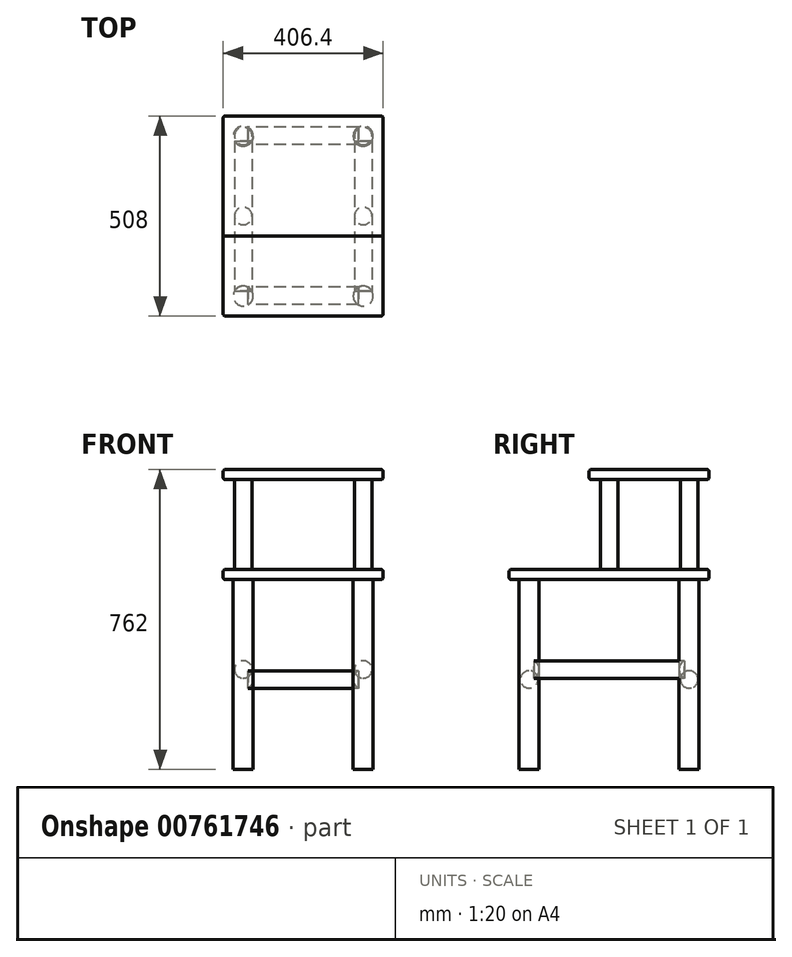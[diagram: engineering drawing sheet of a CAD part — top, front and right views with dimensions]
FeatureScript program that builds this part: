
annotation { "Feature Type Name" : "Feature", "Feature Type Description" : "" }
export const myFeature = defineFeature(function(context is Context, id is Id, definition is map)
    precondition{}
    {
        {
            var Q0;
            Q0=qCreatedBy(makeId("Top.planeOp"),FACE);
            var sketch = newSketch(context, id + "F0", { "sketchPlane" : qUnion([Q0])});
            skLineSegment(sketch, "E0.bottom", {"start": v(152.4, 203.2) * mm, "end": v(-152.4, 203.2) * mm});
            skLineSegment(sketch, "E0.top", {"start": v(152.4, -203.2) * mm, "end": v(-152.4, -203.2) * mm});
            skLineSegment(sketch, "E0.left", {"start": v(152.4, 203.2) * mm, "end": v(152.4, -203.2) * mm});
            skLineSegment(sketch, "E0.right", {"start": v(-152.4, 203.2) * mm, "end": v(-152.4, -203.2) * mm});
            skPoint(sketch, "E0.middle", {"position": v(0, 0) * mm});
            skCircle(sketch, "E1", {"center": v(-152.4, 203.2) * mm, "radius": 25.4 * mm});
            skCircle(sketch, "E2.MirrorC", {"center": v(152.4, 203.2) * mm, "radius": 25.4 * mm});
            skCircle(sketch, "E3.MirrorC", {"center": v(-152.4, -203.2) * mm, "radius": 25.4 * mm});
            skCircle(sketch, "E4.MirrorC", {"center": v(152.4, -203.2) * mm, "radius": 25.4 * mm});
            skSolve(sketch);
        }
        {
            var Q0;
            {var subQ0=sQuery(id+"F0.wireOp",EDGE,"E0.right");var subQ1=sQuery(id+"F0.wireOp",EDGE,"E0.bottom");var subQ2=makeQuery(id+"F0.imprint","INTERSECT",VERTEX,{"derivedFrom":[subQ1,subQ0]});Q0=makeQuery(id+"F0.imprint","IMPRINT",FACE,{"disambiguationData":[TD([[makeQuery(id+"F0.imprint","IMPRINT",EDGE,{"disambiguationData":[TD([[subQ2,1.0]])],"derivedFrom":subQ1}),1.0]])]});}
            var Q1;
            {var subQ0=sQuery(id+"F0.wireOp",EDGE,"E0.right");var subQ1=sQuery(id+"F0.wireOp",EDGE,"E0.bottom");var subQ2=makeQuery(id+"F0.imprint","INTERSECT",VERTEX,{"derivedFrom":[subQ1,subQ0]});Q1=makeQuery(id+"F0.imprint","IMPRINT",FACE,{"disambiguationData":[TD([[makeQuery(id+"F0.imprint","IMPRINT",EDGE,{"disambiguationData":[TD([[subQ2,1.0]])],"derivedFrom":subQ1}),-1.0]])]});}
            var Q2;
            {var subQ0=sQuery(id+"F0.wireOp",EDGE,"E0.left");var subQ1=sQuery(id+"F0.wireOp",EDGE,"E0.bottom");var subQ2=makeQuery(id+"F0.imprint","INTERSECT",VERTEX,{"derivedFrom":[subQ1,subQ0]});Q2=makeQuery(id+"F0.imprint","IMPRINT",FACE,{"disambiguationData":[TD([[makeQuery(id+"F0.imprint","IMPRINT",EDGE,{"disambiguationData":[TD([[subQ2,-1.0]])],"derivedFrom":subQ1}),-1.0]])]});}
            var Q3;
            {var subQ0=sQuery(id+"F0.wireOp",EDGE,"E0.left");var subQ1=sQuery(id+"F0.wireOp",EDGE,"E0.bottom");var subQ2=makeQuery(id+"F0.imprint","INTERSECT",VERTEX,{"derivedFrom":[subQ1,subQ0]});Q3=makeQuery(id+"F0.imprint","IMPRINT",FACE,{"disambiguationData":[TD([[makeQuery(id+"F0.imprint","IMPRINT",EDGE,{"disambiguationData":[TD([[subQ2,-1.0]])],"derivedFrom":subQ1}),1.0]])]});}
            var Q4;
            {var subQ0=sQuery(id+"F0.wireOp",EDGE,"E0.left");var subQ1=sQuery(id+"F0.wireOp",EDGE,"E0.top");var subQ2=makeQuery(id+"F0.imprint","INTERSECT",VERTEX,{"derivedFrom":[subQ1,subQ0]});Q4=makeQuery(id+"F0.imprint","IMPRINT",FACE,{"disambiguationData":[TD([[makeQuery(id+"F0.imprint","IMPRINT",EDGE,{"disambiguationData":[TD([[subQ2,-1.0]])],"derivedFrom":subQ1}),1.0]])]});}
            var Q5;
            {var subQ0=sQuery(id+"F0.wireOp",EDGE,"E0.left");var subQ1=sQuery(id+"F0.wireOp",EDGE,"E0.top");var subQ2=makeQuery(id+"F0.imprint","INTERSECT",VERTEX,{"derivedFrom":[subQ1,subQ0]});Q5=makeQuery(id+"F0.imprint","IMPRINT",FACE,{"disambiguationData":[TD([[makeQuery(id+"F0.imprint","IMPRINT",EDGE,{"disambiguationData":[TD([[subQ2,-1.0]])],"derivedFrom":subQ1}),-1.0]])]});}
            var Q6;
            {var subQ0=sQuery(id+"F0.wireOp",EDGE,"E0.right");var subQ1=sQuery(id+"F0.wireOp",EDGE,"E0.top");var subQ2=makeQuery(id+"F0.imprint","INTERSECT",VERTEX,{"derivedFrom":[subQ1,subQ0]});Q6=makeQuery(id+"F0.imprint","IMPRINT",FACE,{"disambiguationData":[TD([[makeQuery(id+"F0.imprint","IMPRINT",EDGE,{"disambiguationData":[TD([[subQ2,1.0]])],"derivedFrom":subQ1}),-1.0]])]});}
            var Q7;
            {var subQ0=sQuery(id+"F0.wireOp",EDGE,"E0.right");var subQ1=sQuery(id+"F0.wireOp",EDGE,"E0.top");var subQ2=makeQuery(id+"F0.imprint","INTERSECT",VERTEX,{"derivedFrom":[subQ1,subQ0]});Q7=makeQuery(id+"F0.imprint","IMPRINT",FACE,{"disambiguationData":[TD([[makeQuery(id+"F0.imprint","IMPRINT",EDGE,{"disambiguationData":[TD([[subQ2,1.0]])],"derivedFrom":subQ1}),1.0]])]});}
            extrude(context, id + "F1", {"entities" : qUnion([Q0, Q1, Q2, Q3, Q4, Q5, Q6, Q7]), "depth" : 482.6 * mm, "offsetDistance" : 25.4 * mm});
        }
        {
            var Q0;
            Q0=qCreatedBy(makeId("Top.planeOp"),FACE);
            cPlane(context, id + "F2", {"entities" : qUnion([Q0]), "cplaneType" : CPlaneType.OFFSET, "offset" : 482.6 * mm, "width" : 152.4 * mm, "height" : 152.4 * mm});
        }
        {
            var Q0;
            Q0=qCreatedBy(id+"F2.planeOp",FACE);
            var sketch = newSketch(context, id + "F3", { "sketchPlane" : qUnion([Q0])});
            skPoint(sketch, "E5.0", {"position": v(0, 0) * mm});
            skLineSegment(sketch, "E6.bottom", {"start": v(203.2, -254) * mm, "end": v(-203.2, -254) * mm});
            skLineSegment(sketch, "E6.top", {"start": v(203.2, 254) * mm, "end": v(-203.2, 254) * mm});
            skLineSegment(sketch, "E6.left", {"start": v(203.2, -254) * mm, "end": v(203.2, 254) * mm});
            skLineSegment(sketch, "E6.right", {"start": v(-203.2, -254) * mm, "end": v(-203.2, 254) * mm});
            skSolve(sketch);
        }
        {
            var Q0;
            Q0=makeQuery(id+"F3.imprint","IMPRINT",FACE,{"disambiguationData":[TD([[makeQuery(id+"F3.imprint","IMPRINT",EDGE,{"derivedFrom":sQuery(id+"F3.wireOp",EDGE,"E6.bottom")}),-1.0]])]});
            extrude(context, id + "F4", {"entities" : qUnion([Q0]), "depth" : 25.4 * mm, "offsetDistance" : 25.4 * mm});
        }
        {
            var Q0;
            Q0=makeQuery(id+"F4.opExtrude","CAP_FACE",FACE,{"disambiguationData":[OSD([sQuery(id+"F3.wireOp",EDGE,"E6.bottom"),sQuery(id+"F3.wireOp",EDGE,"E6.top"),sQuery(id+"F3.wireOp",EDGE,"E6.left"),sQuery(id+"F3.wireOp",EDGE,"E6.right")])],"isStart":false});
            var sketch = newSketch(context, id + "F5", { "sketchPlane" : qUnion([Q0])});
            skPoint(sketch, "E7.0", {"position": v(152.4, 203.2) * mm});
            skPoint(sketch, "E8.0", {"position": v(-152.4, 203.2) * mm});
            skPoint(sketch, "E9.0", {"position": v(-152.4, -203.2) * mm});
            skPoint(sketch, "E10.0", {"position": v(152.4, -203.2) * mm});
            skLineSegment(sketch, "E11.bottom", {"start": v(152.4, 203.2) * mm, "end": v(-152.4, 203.2) * mm});
            skLineSegment(sketch, "E11.top", {"start": v(152.4, 0) * mm, "end": v(-152.4, 0) * mm});
            skLineSegment(sketch, "E11.left", {"start": v(152.4, 203.2) * mm, "end": v(152.4, 0) * mm});
            skLineSegment(sketch, "E11.right", {"start": v(-152.4, 203.2) * mm, "end": v(-152.4, 0) * mm});
            skCircle(sketch, "E12", {"center": v(152.4, 0) * mm, "radius": 22.23 * mm});
            skCircle(sketch, "E13.MirrorC", {"center": v(-152.4, 0) * mm, "radius": 22.23 * mm});
            skCircle(sketch, "E14", {"center": v(152.4, 203.2) * mm, "radius": 22.23 * mm});
            skCircle(sketch, "E15", {"center": v(-152.4, 203.2) * mm, "radius": 22.23 * mm});
            skSolve(sketch);
        }
        {
            var Q0;
            {var subQ0=sQuery(id+"F5.wireOp",EDGE,"E11.left");var subQ1=sQuery(id+"F5.wireOp",EDGE,"E11.top");var subQ2=makeQuery(id+"F5.imprint","INTERSECT",VERTEX,{"derivedFrom":[subQ1,subQ0]});Q0=makeQuery(id+"F5.imprint","IMPRINT",FACE,{"disambiguationData":[TD([[makeQuery(id+"F5.imprint","IMPRINT",EDGE,{"disambiguationData":[TD([[subQ2,-1.0]])],"derivedFrom":subQ1}),1.0]])]});}
            var Q1;
            {var subQ0=sQuery(id+"F5.wireOp",EDGE,"E11.left");var subQ1=sQuery(id+"F5.wireOp",EDGE,"E11.top");var subQ2=makeQuery(id+"F5.imprint","INTERSECT",VERTEX,{"derivedFrom":[subQ1,subQ0]});Q1=makeQuery(id+"F5.imprint","IMPRINT",FACE,{"disambiguationData":[TD([[makeQuery(id+"F5.imprint","IMPRINT",EDGE,{"disambiguationData":[TD([[subQ2,-1.0]])],"derivedFrom":subQ1}),-1.0]])]});}
            var Q2;
            {var subQ0=sQuery(id+"F5.wireOp",EDGE,"E11.right");var subQ1=sQuery(id+"F5.wireOp",EDGE,"E11.top");var subQ2=makeQuery(id+"F5.imprint","INTERSECT",VERTEX,{"derivedFrom":[subQ1,subQ0]});Q2=makeQuery(id+"F5.imprint","IMPRINT",FACE,{"disambiguationData":[TD([[makeQuery(id+"F5.imprint","IMPRINT",EDGE,{"disambiguationData":[TD([[subQ2,1.0]])],"derivedFrom":subQ1}),-1.0]])]});}
            var Q3;
            {var subQ0=sQuery(id+"F5.wireOp",EDGE,"E11.right");var subQ1=sQuery(id+"F5.wireOp",EDGE,"E11.top");var subQ2=makeQuery(id+"F5.imprint","INTERSECT",VERTEX,{"derivedFrom":[subQ1,subQ0]});Q3=makeQuery(id+"F5.imprint","IMPRINT",FACE,{"disambiguationData":[TD([[makeQuery(id+"F5.imprint","IMPRINT",EDGE,{"disambiguationData":[TD([[subQ2,1.0]])],"derivedFrom":subQ1}),1.0]])]});}
            var Q4;
            {var subQ0=sQuery(id+"F5.wireOp",EDGE,"E11.right");var subQ1=sQuery(id+"F5.wireOp",EDGE,"E11.bottom");var subQ2=makeQuery(id+"F5.imprint","INTERSECT",VERTEX,{"derivedFrom":[subQ1,subQ0]});Q4=makeQuery(id+"F5.imprint","IMPRINT",FACE,{"disambiguationData":[TD([[makeQuery(id+"F5.imprint","IMPRINT",EDGE,{"disambiguationData":[TD([[subQ2,1.0]])],"derivedFrom":subQ1}),-1.0]])]});}
            var Q5;
            {var subQ0=sQuery(id+"F5.wireOp",EDGE,"E11.right");var subQ1=sQuery(id+"F5.wireOp",EDGE,"E11.bottom");var subQ2=makeQuery(id+"F5.imprint","INTERSECT",VERTEX,{"derivedFrom":[subQ1,subQ0]});Q5=makeQuery(id+"F5.imprint","IMPRINT",FACE,{"disambiguationData":[TD([[makeQuery(id+"F5.imprint","IMPRINT",EDGE,{"disambiguationData":[TD([[subQ2,1.0]])],"derivedFrom":subQ1}),1.0]])]});}
            var Q6;
            {var subQ0=sQuery(id+"F5.wireOp",EDGE,"E11.left");var subQ1=sQuery(id+"F5.wireOp",EDGE,"E11.bottom");var subQ2=makeQuery(id+"F5.imprint","INTERSECT",VERTEX,{"derivedFrom":[subQ1,subQ0]});Q6=makeQuery(id+"F5.imprint","IMPRINT",FACE,{"disambiguationData":[TD([[makeQuery(id+"F5.imprint","IMPRINT",EDGE,{"disambiguationData":[TD([[subQ2,-1.0]])],"derivedFrom":subQ1}),1.0]])]});}
            var Q7;
            {var subQ0=sQuery(id+"F5.wireOp",EDGE,"E11.left");var subQ1=sQuery(id+"F5.wireOp",EDGE,"E11.bottom");var subQ2=makeQuery(id+"F5.imprint","INTERSECT",VERTEX,{"derivedFrom":[subQ1,subQ0]});Q7=makeQuery(id+"F5.imprint","IMPRINT",FACE,{"disambiguationData":[TD([[makeQuery(id+"F5.imprint","IMPRINT",EDGE,{"disambiguationData":[TD([[subQ2,-1.0]])],"derivedFrom":subQ1}),-1.0]])]});}
            extrude(context, id + "F6", {"entities" : qUnion([Q0, Q1, Q2, Q3, Q4, Q5, Q6, Q7]), "depth" : 228.6 * mm, "offsetDistance" : 25.4 * mm});
        }
        {
            var Q0;
            Q0=makeQuery(id+"F6.opExtrude","CAP_FACE",FACE,{"disambiguationData":[OSD([sQuery(id+"F5.wireOp",EDGE,"E12")])],"isStart":false});
            var sketch = newSketch(context, id + "F7", { "sketchPlane" : qUnion([Q0])});
            skPoint(sketch, "E16.0", {"position": v(152.4, 203.2) * mm});
            skPoint(sketch, "E17.0", {"position": v(152.4, 0) * mm});
            skPoint(sketch, "E18.0", {"position": v(-152.4, 0) * mm});
            skPoint(sketch, "E19.0", {"position": v(-152.4, 203.2) * mm});
            skLineSegment(sketch, "E20", {"start": v(152.4, 0) * mm, "end": v(152.4, 203.2) * mm});
            skLineSegment(sketch, "E21.bottom", {"start": v(-203.2, 254) * mm, "end": v(203.2, 254) * mm});
            skLineSegment(sketch, "E21.top", {"start": v(-203.2, -50.8) * mm, "end": v(203.2, -50.8) * mm});
            skLineSegment(sketch, "E21.left", {"start": v(-203.2, 254) * mm, "end": v(-203.2, -50.8) * mm});
            skLineSegment(sketch, "E21.right", {"start": v(203.2, 254) * mm, "end": v(203.2, -50.8) * mm});
            skPoint(sketch, "E21.middle", {"position": v(0, 101.6) * mm});
            skPoint(sketch, "E21.middle.positionSnap0", {"position": v(152.4, 101.6) * mm});
            skPoint(sketch, "E21.centerSnap0", {"position": v(152.4, 101.6) * mm});
            skSolve(sketch);
        }
        {
            var Q0;
            Q0 = qSketchRegion(id + "F7", true);
            extrude(context, id + "F8", {"entities" : qUnion([Q0]), "depth" : 25.4 * mm, "offsetDistance" : 25.4 * mm});
        }
        {
            var Q0;
            Q0=makeQuery(id+"F4.opExtrude","SWEPT_EDGE",EDGE,{"disambiguationData":[OSD([sQuery(id+"F3.wireOp",EDGE,"E6.bottom"),sQuery(id+"F3.wireOp",EDGE,"E6.right")])]});
            var Q1;
            Q1=makeQuery(id+"F4.opExtrude","CAP_EDGE",EDGE,{"disambiguationData":[OSD([sQuery(id+"F3.wireOp",EDGE,"E6.bottom")])],"isStart":false});
            var Q2;
            Q2=makeQuery(id+"F4.opExtrude","CAP_EDGE",EDGE,{"disambiguationData":[OSD([sQuery(id+"F3.wireOp",EDGE,"E6.bottom")])],"isStart":true});
            var Q3;
            Q3=makeQuery(id+"F4.opExtrude","CAP_EDGE",EDGE,{"disambiguationData":[OSD([sQuery(id+"F3.wireOp",EDGE,"E6.right")])],"isStart":false});
            var Q4;
            Q4=makeQuery(id+"F4.opExtrude","CAP_EDGE",EDGE,{"disambiguationData":[OSD([sQuery(id+"F3.wireOp",EDGE,"E6.right")])],"isStart":true});
            var Q5;
            Q5=makeQuery(id+"F4.opExtrude","SWEPT_EDGE",EDGE,{"disambiguationData":[OSD([sQuery(id+"F3.wireOp",EDGE,"E6.bottom"),sQuery(id+"F3.wireOp",EDGE,"E6.left")])]});
            var Q6;
            Q6=makeQuery(id+"F4.opExtrude","CAP_EDGE",EDGE,{"disambiguationData":[OSD([sQuery(id+"F3.wireOp",EDGE,"E6.left")])],"isStart":false});
            var Q7;
            Q7=makeQuery(id+"F4.opExtrude","CAP_EDGE",EDGE,{"disambiguationData":[OSD([sQuery(id+"F3.wireOp",EDGE,"E6.left")])],"isStart":true});
            var Q8;
            Q8=makeQuery(id+"F4.opExtrude","SWEPT_EDGE",EDGE,{"disambiguationData":[OSD([sQuery(id+"F3.wireOp",EDGE,"E6.top"),sQuery(id+"F3.wireOp",EDGE,"E6.left")])]});
            var Q9;
            Q9=makeQuery(id+"F4.opExtrude","CAP_EDGE",EDGE,{"disambiguationData":[OSD([sQuery(id+"F3.wireOp",EDGE,"E6.top")])],"isStart":true});
            var Q10;
            Q10=makeQuery(id+"F4.opExtrude","CAP_EDGE",EDGE,{"disambiguationData":[OSD([sQuery(id+"F3.wireOp",EDGE,"E6.top")])],"isStart":false});
            var Q11;
            Q11=makeQuery(id+"F4.opExtrude","SWEPT_EDGE",EDGE,{"disambiguationData":[OSD([sQuery(id+"F3.wireOp",EDGE,"E6.top"),sQuery(id+"F3.wireOp",EDGE,"E6.right")])]});
            fillet(context, id + "F9", {"entities" : qUnion([Q0, Q1, Q2, Q3, Q4, Q5, Q6, Q7, Q8, Q9, Q10, Q11]), "radius" : 5.08 * mm, "tangentPropagation" : true, "allowEdgeOverflow" : false});
        }
        {
            var Q0;
            Q0=makeQuery(id+"F8.opExtrude","SWEPT_EDGE",EDGE,{"disambiguationData":[OSD([sQuery(id+"F7.wireOp",EDGE,"E21.bottom"),sQuery(id+"F7.wireOp",EDGE,"E21.left")])]});
            var Q1;
            Q1=makeQuery(id+"F8.opExtrude","CAP_EDGE",EDGE,{"disambiguationData":[OSD([sQuery(id+"F7.wireOp",EDGE,"E21.bottom")])],"isStart":true});
            var Q2;
            Q2=makeQuery(id+"F8.opExtrude","CAP_EDGE",EDGE,{"disambiguationData":[OSD([sQuery(id+"F7.wireOp",EDGE,"E21.left")])],"isStart":true});
            var Q3;
            Q3=makeQuery(id+"F8.opExtrude","CAP_EDGE",EDGE,{"disambiguationData":[OSD([sQuery(id+"F7.wireOp",EDGE,"E21.left")])],"isStart":false});
            var Q4;
            Q4=makeQuery(id+"F8.opExtrude","CAP_EDGE",EDGE,{"disambiguationData":[OSD([sQuery(id+"F7.wireOp",EDGE,"E21.bottom")])],"isStart":false});
            var Q5;
            Q5=makeQuery(id+"F8.opExtrude","SWEPT_EDGE",EDGE,{"disambiguationData":[OSD([sQuery(id+"F7.wireOp",EDGE,"E21.bottom"),sQuery(id+"F7.wireOp",EDGE,"E21.right")])]});
            var Q6;
            Q6=makeQuery(id+"F8.opExtrude","CAP_EDGE",EDGE,{"disambiguationData":[OSD([sQuery(id+"F7.wireOp",EDGE,"E21.right")])],"isStart":true});
            var Q7;
            Q7=makeQuery(id+"F8.opExtrude","CAP_EDGE",EDGE,{"disambiguationData":[OSD([sQuery(id+"F7.wireOp",EDGE,"E21.right")])],"isStart":false});
            var Q8;
            Q8=makeQuery(id+"F8.opExtrude","SWEPT_EDGE",EDGE,{"disambiguationData":[OSD([sQuery(id+"F7.wireOp",EDGE,"E21.top"),sQuery(id+"F7.wireOp",EDGE,"E21.right")])]});
            var Q9;
            Q9=makeQuery(id+"F8.opExtrude","CAP_EDGE",EDGE,{"disambiguationData":[OSD([sQuery(id+"F7.wireOp",EDGE,"E21.top")])],"isStart":false});
            var Q10;
            Q10=makeQuery(id+"F8.opExtrude","CAP_EDGE",EDGE,{"disambiguationData":[OSD([sQuery(id+"F7.wireOp",EDGE,"E21.top")])],"isStart":true});
            var Q11;
            Q11=makeQuery(id+"F8.opExtrude","SWEPT_EDGE",EDGE,{"disambiguationData":[OSD([sQuery(id+"F7.wireOp",EDGE,"E21.top"),sQuery(id+"F7.wireOp",EDGE,"E21.left")])]});
            fillet(context, id + "F10", {"entities" : qUnion([Q0, Q1, Q2, Q3, Q4, Q5, Q6, Q7, Q8, Q9, Q10, Q11]), "radius" : 5.08 * mm, "tangentPropagation" : true, "allowEdgeOverflow" : false});
        }
        {
            var Q0;
            Q0=qCreatedBy(makeId("Top.planeOp"),FACE);
            cPlane(context, id + "F11", {"entities" : qUnion([Q0]), "cplaneType" : CPlaneType.OFFSET, "offset" : 254 * mm, "width" : 152.4 * mm, "height" : 152.4 * mm});
        }
        {
            var Q0;
            Q0=qCreatedBy(id+"F11.planeOp",FACE);
            var sketch = newSketch(context, id + "F12", { "sketchPlane" : qUnion([Q0])});
            skCircle(sketch, "E22.0", {"center": v(-152.4, -203.2) * mm, "radius": 25.4 * mm});
            skCircle(sketch, "E23.0", {"center": v(152.4, -203.2) * mm, "radius": 25.4 * mm});
            skCircle(sketch, "E24.0", {"center": v(-152.4, 203.2) * mm, "radius": 25.4 * mm});
            skCircle(sketch, "E25.0", {"center": v(152.4, 203.2) * mm, "radius": 25.4 * mm});
            skLineSegment(sketch, "E26", {"start": v(-152.4, -203.2) * mm, "end": v(-152.4, 203.2) * mm});
            skLineSegment(sketch, "E27", {"start": v(152.4, -203.2) * mm, "end": v(152.4, 203.2) * mm});
            skLineSegment(sketch, "E28", {"start": v(-152.4, -203.2) * mm, "end": v(-130.17, -203.2) * mm});
            skLineSegment(sketch, "E29", {"start": v(-152.4, -203.2) * mm, "end": v(-174.62, -203.2) * mm});
            skLineSegment(sketch, "E30", {"start": v(-174.62, -203.2) * mm, "end": v(-174.62, 190.9) * mm});
            skLineSegment(sketch, "E31", {"start": v(-174.62, 190.9) * mm, "end": v(-130.17, 190.9) * mm});
            skLineSegment(sketch, "E32", {"start": v(-130.17, 190.9) * mm, "end": v(-130.17, -203.2) * mm});
            skLineSegment(sketch, "E33.MirrorCS", {"start": v(174.62, -203.2) * mm, "end": v(174.62, 190.9) * mm});
            skLineSegment(sketch, "E34.MirrorCS", {"start": v(130.17, 190.9) * mm, "end": v(130.17, -203.2) * mm});
            skSolve(sketch);
        }
        {
            var Q0;
            {var subQ0=sQuery(id+"F12.wireOp",EDGE,"E30");var subQ1=sQuery(id+"F12.wireOp",EDGE,"E22.0");var subQ2=makeQuery(id+"F12.imprint","INTERSECT",VERTEX,{"derivedFrom":[subQ1,subQ0]});Q0=makeQuery(id+"F12.imprint","IMPRINT",FACE,{"disambiguationData":[TD([[makeQuery(id+"F12.imprint","IMPRINT",EDGE,{"disambiguationData":[TD([[subQ2,1.0]])],"derivedFrom":subQ1}),-1.0]])]});}
            var Q1;
            Q1=sQuery(id+"F12.wireOp",EDGE,"E26");
            revolve(context, id + "F13", {"surfaceOperationType" : NewSurfaceOperationType.NEW, "entities" : qUnion([Q0]), "axis" : qUnion([Q1]), "revolveType" : RevolveType.FULL});
        }
        {
            var Q0;
            {var subQ0=sQuery(id+"F12.wireOp",EDGE,"E34.MirrorCS");var subQ1=sQuery(id+"F12.wireOp",EDGE,"E23.0");var subQ2=makeQuery(id+"F12.imprint","INTERSECT",VERTEX,{"derivedFrom":[subQ1,subQ0]});Q0=makeQuery(id+"F12.imprint","IMPRINT",FACE,{"disambiguationData":[TD([[makeQuery(id+"F12.imprint","IMPRINT",EDGE,{"disambiguationData":[TD([[subQ2,1.0]])],"derivedFrom":subQ1}),-1.0]])]});}
            var Q1;
            Q1=sQuery(id+"F12.wireOp",EDGE,"E27");
            revolve(context, id + "F14", {"surfaceOperationType" : NewSurfaceOperationType.NEW, "entities" : qUnion([Q0]), "axis" : qUnion([Q1]), "revolveType" : RevolveType.FULL});
        }
        {
            var Q0;
            Q0=qCreatedBy(makeId("Top.planeOp"),FACE);
            cPlane(context, id + "F15", {"entities" : qUnion([Q0]), "cplaneType" : CPlaneType.OFFSET, "offset" : 228.6 * mm, "width" : 152.4 * mm, "height" : 152.4 * mm});
        }
        {
            var Q0;
            Q0=qCreatedBy(id+"F15.planeOp",FACE);
            var sketch = newSketch(context, id + "F16", { "sketchPlane" : qUnion([Q0])});
            skCircle(sketch, "E35.0", {"center": v(-152.4, -203.2) * mm, "radius": 25.4 * mm});
            skCircle(sketch, "E36.0", {"center": v(152.4, -203.2) * mm, "radius": 25.4 * mm});
            skCircle(sketch, "E37.0", {"center": v(152.4, 203.2) * mm, "radius": 25.4 * mm});
            skCircle(sketch, "E38.0", {"center": v(-152.4, 203.2) * mm, "radius": 25.4 * mm});
            skLineSegment(sketch, "E39", {"start": v(-152.4, -203.2) * mm, "end": v(152.4, -203.2) * mm});
            skLineSegment(sketch, "E40", {"start": v(-152.4, 203.2) * mm, "end": v(152.4, 203.2) * mm});
            skLineSegment(sketch, "E41", {"start": v(-152.4, 203.2) * mm, "end": v(-152.4, 180.98) * mm});
            skLineSegment(sketch, "E42", {"start": v(-152.4, 180.98) * mm, "end": v(140.1, 180.98) * mm});
            skLineSegment(sketch, "E43.MirrorCS", {"start": v(-152.4, -180.98) * mm, "end": v(140.1, -180.98) * mm});
            skSolve(sketch);
        }
        {
            var Q0;
            {var subQ0=sQuery(id+"F16.wireOp",EDGE,"E42");var subQ1=sQuery(id+"F16.wireOp",EDGE,"E37.0");var subQ2=makeQuery(id+"F16.imprint","INTERSECT",VERTEX,{"derivedFrom":[subQ1,subQ0]});Q0=makeQuery(id+"F16.imprint","IMPRINT",FACE,{"disambiguationData":[TD([[makeQuery(id+"F16.imprint","IMPRINT",EDGE,{"disambiguationData":[TD([[subQ2,1.0]])],"derivedFrom":subQ1}),-1.0]])]});}
            var Q1;
            Q1=sQuery(id+"F16.wireOp",EDGE,"E40");
            revolve(context, id + "F17", {"surfaceOperationType" : NewSurfaceOperationType.NEW, "entities" : qUnion([Q0]), "axis" : qUnion([Q1]), "revolveType" : RevolveType.FULL});
        }
        {
            var Q0;
            {var subQ0=sQuery(id+"F16.wireOp",EDGE,"E43.MirrorCS");var subQ1=sQuery(id+"F16.wireOp",EDGE,"E35.0");var subQ2=makeQuery(id+"F16.imprint","INTERSECT",VERTEX,{"derivedFrom":[subQ1,subQ0]});Q0=makeQuery(id+"F16.imprint","IMPRINT",FACE,{"disambiguationData":[TD([[makeQuery(id+"F16.imprint","IMPRINT",EDGE,{"disambiguationData":[TD([[subQ2,1.0]])],"derivedFrom":subQ1}),-1.0]])]});}
            var Q1;
            Q1=sQuery(id+"F16.wireOp",EDGE,"E39");
            revolve(context, id + "F18", {"surfaceOperationType" : NewSurfaceOperationType.NEW, "entities" : qUnion([Q0]), "axis" : qUnion([Q1]), "revolveType" : RevolveType.FULL});
        }
    });
